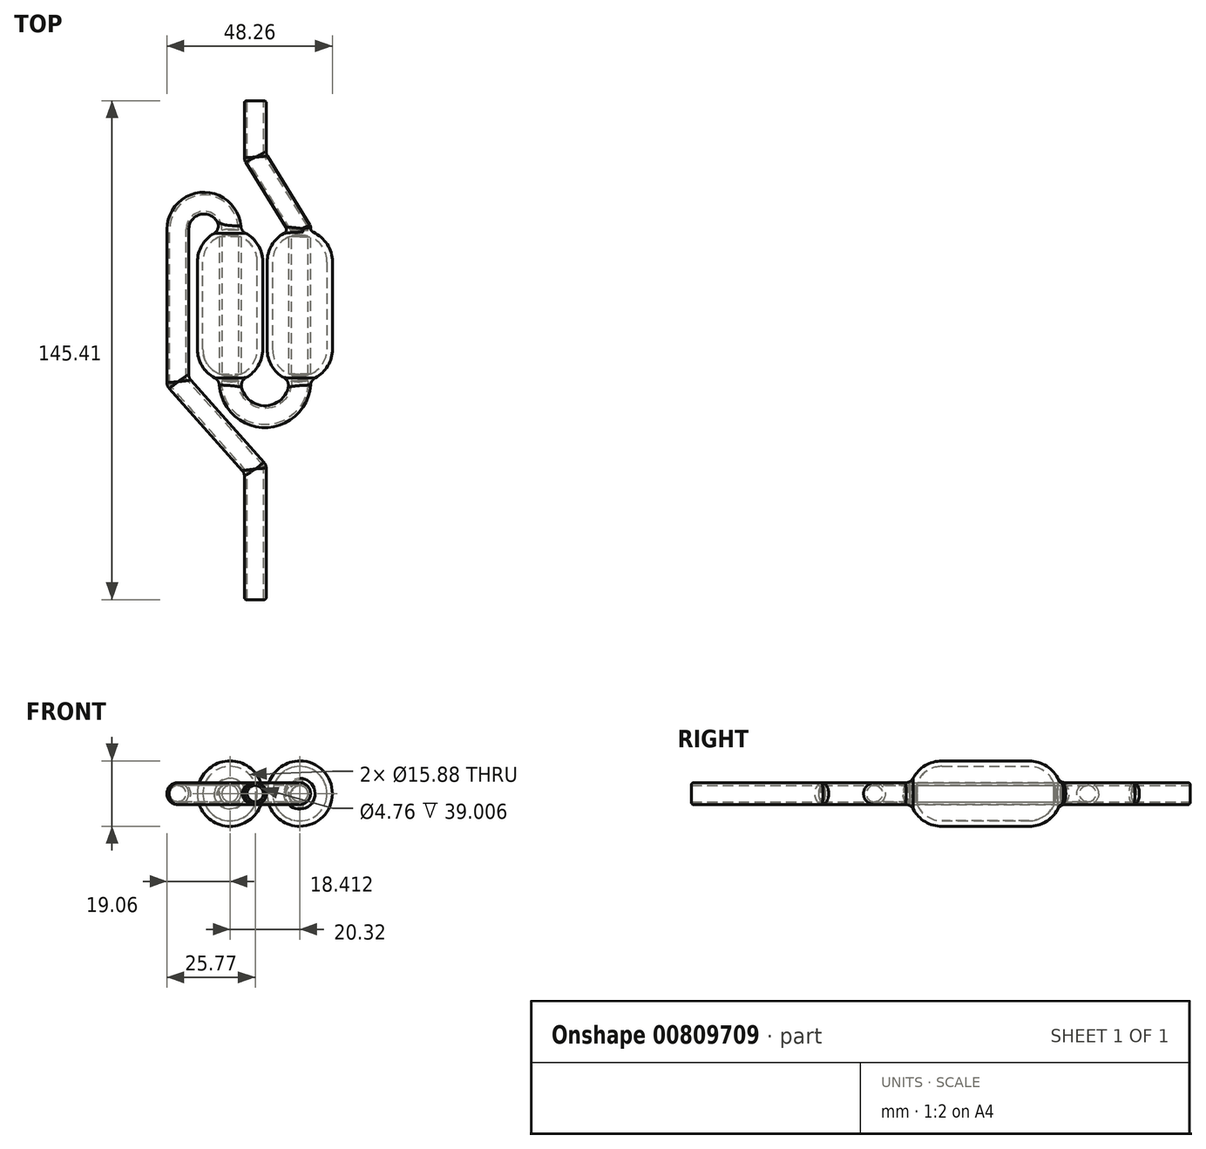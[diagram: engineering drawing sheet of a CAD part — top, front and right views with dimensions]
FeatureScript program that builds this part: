
annotation { "Feature Type Name" : "Feature", "Feature Type Description" : "" }
export const myFeature = defineFeature(function(context is Context, id is Id, definition is map)
    precondition{}
    {
        {
            var Q0;
            Q0=qCreatedBy(makeId("Top.planeOp"),FACE);
            var sketch = newSketch(context, id + "F0", { "sketchPlane" : qUnion([Q0])});
            skLineSegment(sketch, "E0", {"start": v(0, -39.55) * mm, "end": v(0, -1.45) * mm});
            skLineSegment(sketch, "E1", {"start": v(0, -1.45) * mm, "end": v(-22.6, 23.95) * mm});
            skLineSegment(sketch, "E2", {"start": v(-22.6, 23.95) * mm, "end": v(-22.6, 68.4) * mm});
            skLineSegment(sketch, "E3", {"start": v(-7.36, 68.4) * mm, "end": v(-7.36, 23.95) * mm});
            skLineSegment(sketch, "E4", {"start": v(12.96, 23.95) * mm, "end": v(12.96, 68.4) * mm});
            skLineSegment(sketch, "E5", {"start": v(12.96, 68.4) * mm, "end": v(0, 89.43) * mm});
            skLineSegment(sketch, "E6", {"start": v(0, 89.43) * mm, "end": v(0, 105.86) * mm});
            skLineSegment(sketch, "E7", {"start": v(-22.6, 23.95) * mm, "end": v(-14.25, 23.95) * mm, "construction": true});
            skPoint(sketch, "E8.visualSharp", {"position": v(-22.6, 80.08) * mm});
            skArc(sketch, "E8.filletArc", {"start": v(-14.98, 76.02) * mm, "mid": v(-20.37, 73.79) * mm, "end": v(-22.6, 68.4) * mm});
            skPoint(sketch, "E9.visualSharp", {"position": v(-7.36, 76.07) * mm});
            skPoint(sketch, "E10.visualSharp", {"position": v(-14.25, 23.95) * mm});
            skPoint(sketch, "E11.visualSharp", {"position": v(12.96, 3.76) * mm});
            skLineSegment(sketch, "E12", {"start": v(2.17, 58.87) * mm, "end": v(2.17, 33.47) * mm});
            skLineSegment(sketch, "E13", {"start": v(0.58, 58.87) * mm, "end": v(0.58, 33.47) * mm});
            skPoint(sketch, "E14.start.orphan", {"position": v(-14.56, 68.4) * mm});
            skPoint(sketch, "E15.orphan", {"position": v(-13.66, 23.95) * mm});
            skLineSegment(sketch, "E16", {"start": v(12.96, 23.95) * mm, "end": v(12.96, 8.24) * mm, "construction": true});
            skLineSegment(sketch, "E17", {"start": v(12.96, 23.95) * mm, "end": v(20.36, 23.95) * mm, "construction": true});
            skPoint(sketch, "E18.start.orphan", {"position": v(5.98, 68.4) * mm});
            skPoint(sketch, "E19.orphan", {"position": v(7.66, 23.95) * mm});
            skArc(sketch, "E20", {"start": v(-7.36, 23.95) * mm, "mid": v(-0.62, 26.74) * mm, "end": v(2.17, 33.47) * mm});
            skArc(sketch, "E21", {"start": v(0.58, 33.47) * mm, "mid": v(-1.75, 27.86) * mm, "end": v(-7.36, 25.54) * mm});
            skArc(sketch, "E22", {"start": v(-7.36, 68.4) * mm, "mid": v(-0.62, 65.61) * mm, "end": v(2.17, 58.87) * mm});
            skArc(sketch, "E23", {"start": v(0.58, 58.87) * mm, "mid": v(-1.75, 64.49) * mm, "end": v(-7.36, 66.81) * mm});
            skPoint(sketch, "E24.orphan", {"position": v(2.17, 23.95) * mm});
            skPoint(sketch, "E25.orphan", {"position": v(0.58, 68.4) * mm});
            skPoint(sketch, "E26.end.orphan", {"position": v(2.17, 68.4) * mm});
            skLineSegment(sketch, "E27", {"start": v(-7.36, 33.47) * mm, "end": v(0, 33.47) * mm, "construction": true});
            skLineSegment(sketch, "E28", {"start": v(-7.36, 58.87) * mm, "end": v(0, 58.87) * mm, "construction": true});
            skLineSegment(sketch, "E29", {"start": v(12.96, 68.4) * mm, "end": v(12.96, 23.95) * mm});
            skLineSegment(sketch, "E30", {"start": v(22.49, 58.87) * mm, "end": v(22.49, 33.47) * mm});
            skLineSegment(sketch, "E31", {"start": v(20.9, 58.87) * mm, "end": v(20.9, 33.47) * mm});
            skArc(sketch, "E32", {"start": v(12.96, 23.95) * mm, "mid": v(19.7, 26.74) * mm, "end": v(22.49, 33.47) * mm});
            skArc(sketch, "E33", {"start": v(20.9, 33.47) * mm, "mid": v(18.57, 27.86) * mm, "end": v(12.96, 25.54) * mm});
            skArc(sketch, "E34", {"start": v(12.96, 68.4) * mm, "mid": v(19.7, 65.61) * mm, "end": v(22.49, 58.87) * mm});
            skArc(sketch, "E35", {"start": v(20.9, 58.87) * mm, "mid": v(18.57, 64.49) * mm, "end": v(12.96, 66.81) * mm});
            skPoint(sketch, "E36.orphan", {"position": v(22.49, 23.95) * mm});
            skPoint(sketch, "E37.orphan", {"position": v(20.9, 68.4) * mm});
            skPoint(sketch, "E38.end.orphan", {"position": v(22.49, 68.4) * mm});
            skLineSegment(sketch, "E39", {"start": v(12.96, 33.47) * mm, "end": v(20.32, 33.47) * mm, "construction": true});
            skLineSegment(sketch, "E40", {"start": v(12.96, 58.87) * mm, "end": v(20.32, 58.87) * mm, "construction": true});
            skPoint(sketch, "E41.start.orphan", {"position": v(18.68, 68.4) * mm});
            skArc(sketch, "E42", {"start": v(-14.98, 76.02) * mm, "mid": v(-9.6, 73.79) * mm, "end": v(-7.36, 68.4) * mm});
            skPoint(sketch, "E43.end.orphan", {"position": v(-14.98, 76.02) * mm});
            skLineSegment(sketch, "E44", {"start": v(-7.36, 23.95) * mm, "end": v(-22.6, 23.95) * mm, "construction": true});
            skArc(sketch, "E45.MirrorCS", {"start": v(2.8, 13.79) * mm, "mid": v(-4.38, 16.77) * mm, "end": v(-7.36, 23.95) * mm});
            skArc(sketch, "E46.MirrorCS", {"start": v(2.8, 13.79) * mm, "mid": v(9.99, 16.77) * mm, "end": v(12.96, 23.95) * mm});
            skLineSegment(sketch, "E47", {"start": v(-7.36, 23.95) * mm, "end": v(46.58, 23.95) * mm, "construction": true});
            skLineSegment(sketch, "E48", {"start": v(0, 0) * mm, "end": v(0, 151.72) * mm, "construction": true});
            skSolve(sketch);
        }
        {
            var Q0;
            Q0=qCreatedBy(makeId("Front.planeOp"),FACE);
            var Q1;
            Q1=sQuery(id+"F0.wireOp",VERTEX,"E0.start");
            cPlane(context, id + "F1", {"entities" : qUnion([Q0, Q1]), "cplaneType" : CPlaneType.PLANE_POINT, "offset" : 25.4 * mm, "width" : 152.4 * mm, "height" : 152.4 * mm});
        }
        {
            var Q0;
            Q0=qCreatedBy(id+"F1.planeOp",FACE);
            var sketch = newSketch(context, id + "F2", { "sketchPlane" : qUnion([Q0])});
            skCircle(sketch, "E49", {"center": v(0, 0) * mm, "radius": 3.18 * mm});
            skCircle(sketch, "E50", {"center": v(0, 0) * mm, "radius": 2.38 * mm});
            skSolve(sketch);
        }
        {
            var Q0;
            Q0=makeQuery(id+"F2.imprint","IMPRINT",FACE,{"disambiguationData":[TD([[makeQuery(id+"F2.imprint","IMPRINT",EDGE,{"derivedFrom":sQuery(id+"F2.wireOp",EDGE,"E49")}),1.0]])]});
            var Q1;
            Q1=sQuery(id+"F0.wireOp",EDGE,"E0");
            var Q2;
            Q2=sQuery(id+"F0.wireOp",EDGE,"E1");
            var Q3;
            Q3=sQuery(id+"F0.wireOp",EDGE,"E2");
            var Q4;
            Q4=sQuery(id+"F0.wireOp",EDGE,"E8.filletArc");
            var Q5;
            Q5=sQuery(id+"F0.wireOp",EDGE,"E43");
            var Q6;
            Q6=sQuery(id+"F0.wireOp",EDGE,"E9.filletArc");
            var Q7;
            Q7=sQuery(id+"F0.wireOp",EDGE,"E3");
            var Q8;
            Q8=sQuery(id+"F0.wireOp",EDGE,"E10.filletArc");
            var Q9;
            Q9=sQuery(id+"F0.wireOp",EDGE,"5njKzUmd-qnUo-V2Rh-gXgK-mwkRtPWxnCq9");
            var Q10;
            Q10=sQuery(id+"F0.wireOp",EDGE,"E11.filletArc");
            var Q11;
            Q11=sQuery(id+"F0.wireOp",EDGE,"E4");
            var Q12;
            Q12=sQuery(id+"F0.wireOp",EDGE,"E5");
            var Q13;
            Q13=sQuery(id+"F0.wireOp",EDGE,"E6");
            var Q14;
            Q14=sQuery(id+"F0.wireOp",EDGE,"E42");
            var Q15;
            Q15=sQuery(id+"F0.wireOp",EDGE,"E45.MirrorCS");
            var Q16;
            Q16=sQuery(id+"F0.wireOp",EDGE,"E46.MirrorCS");
            sweep(context, id + "F3", {"profiles" : qUnion([Q0]), "path" : qUnion([Q1, Q2, Q3, Q4, Q5, Q6, Q7, Q8, Q9, Q10, Q11, Q12, Q13, Q14, Q15, Q16])});
        }
        {
            var Q0;
            {var subQ0=sQuery(id+"F0.wireOp",EDGE,"E26");Q0=makeQuery(id+"F0.imprint","IMPRINT",FACE,{"disambiguationData":[TD([[makeQuery(id+"F0.imprint","IMPRINT",EDGE,{"derivedFrom":subQ0}),-1.0]])]});}
            var Q1;
            Q1=makeQuery(id+"F0.imprint","IMPRINT",FACE,{"disambiguationData":[TD([[makeQuery(id+"F0.imprint","IMPRINT",EDGE,{"derivedFrom":sQuery(id+"F0.wireOp",EDGE,"E12")}),-1.0]])]});
            var Q2;
            Q2=sQuery(id+"F0.wireOp",EDGE,"E3");
            revolve(context, id + "F4", {"operationType" : NewBodyOperationType.ADD, "surfaceOperationType" : NewSurfaceOperationType.NEW, "entities" : qUnion([Q0, Q1]), "axis" : qUnion([Q2]), "revolveType" : RevolveType.FULL});
        }
        {
            var Q0;
            Q0=makeQuery(id+"F0.imprint","IMPRINT",FACE,{"disambiguationData":[TD([[makeQuery(id+"F0.imprint","IMPRINT",EDGE,{"derivedFrom":sQuery(id+"F0.wireOp",EDGE,"E30")}),-1.0]])]});
            var Q1;
            Q1=sQuery(id+"F0.wireOp",EDGE,"E4");
            revolve(context, id + "F5", {"operationType" : NewBodyOperationType.ADD, "surfaceOperationType" : NewSurfaceOperationType.NEW, "entities" : qUnion([Q0]), "axis" : qUnion([Q1]), "revolveType" : RevolveType.FULL});
        }
        {
            var Q0;
            Q0=makeQuery(id+"F4.boolean.opBoolean","INTERSECT",EDGE,{"derivedFrom":[makeQuery(id+"F3.opSweep","SWEPT_FACE",FACE,{"disambiguationData":[OSD([sQuery(id+"F0.wireOp",EDGE,"E3"),sQuery(id+"F2.wireOp",EDGE,"E49")])]}),makeQuery(id+"F4.opRevolve","SWEPT_FACE",FACE,{"disambiguationData":[OSD([sQuery(id+"F0.wireOp",EDGE,"E22")])]})]});
            var Q1;
            Q1=makeQuery(id+"F4.boolean.opBoolean","INTERSECT",EDGE,{"derivedFrom":[makeQuery(id+"F3.opSweep","SWEPT_FACE",FACE,{"disambiguationData":[OSD([sQuery(id+"F0.wireOp",EDGE,"E3"),sQuery(id+"F2.wireOp",EDGE,"E49")])]}),makeQuery(id+"F4.opRevolve","SWEPT_FACE",FACE,{"disambiguationData":[OSD([sQuery(id+"F0.wireOp",EDGE,"E20")])]})]});
            var Q2;
            Q2=makeQuery(id+"F5.boolean.opBoolean","INTERSECT",EDGE,{"derivedFrom":[makeQuery(id+"F3.opSweep","SWEPT_FACE",FACE,{"disambiguationData":[OSD([sQuery(id+"F0.wireOp",EDGE,"E4"),sQuery(id+"F2.wireOp",EDGE,"E49")])]}),makeQuery(id+"F5.opRevolve","SWEPT_FACE",FACE,{"disambiguationData":[OSD([sQuery(id+"F0.wireOp",EDGE,"E32")])]})]});
            var Q3;
            Q3=makeQuery(id+"F3.opSweep","MID_CAP_EDGE",EDGE,{"disambiguationData":[OSD([sQuery(id+"F0.wireOp",VERTEX,"E2.start"),sQuery(id+"F2.wireOp",EDGE,"E49")])],"capPos":2.0});
            var Q4;
            Q4=makeQuery(id+"F3.opSweep","MID_CAP_EDGE",EDGE,{"disambiguationData":[OSD([sQuery(id+"F0.wireOp",VERTEX,"E1.start"),sQuery(id+"F2.wireOp",EDGE,"E49")])],"capPos":1.0});
            var Q5;
            Q5=makeQuery(id+"F3.opSweep","MID_CAP_EDGE",EDGE,{"disambiguationData":[OSD([sQuery(id+"F0.wireOp",VERTEX,"E6.start"),sQuery(id+"F2.wireOp",EDGE,"E49")])],"capPos":10.0});
            fillet(context, id + "F6", {"entities" : qUnion([Q0, Q1, Q2, Q3, Q4, Q5]), "radius" : 2.54 * mm, "tangentPropagation" : true, "allowEdgeOverflow" : false});
        }
        {
            var Q0;
            Q0=makeQuery(id+"F5.boolean.opBoolean","INTERSECT",EDGE,{"derivedFrom":[makeQuery(id+"F3.opSweep","SWEPT_FACE",FACE,{"disambiguationData":[OSD([sQuery(id+"F0.wireOp",EDGE,"E5"),sQuery(id+"F2.wireOp",EDGE,"E49")])]}),makeQuery(id+"F5.opRevolve","SWEPT_FACE",FACE,{"disambiguationData":[OSD([sQuery(id+"F0.wireOp",EDGE,"E34")])]})]});
            var Q1;
            Q1=makeQuery(id+"F5.boolean.opBoolean","INTERSECT",EDGE,{"derivedFrom":[makeQuery(id+"F3.opSweep","SWEPT_FACE",FACE,{"disambiguationData":[OSD([sQuery(id+"F0.wireOp",EDGE,"E4"),sQuery(id+"F2.wireOp",EDGE,"E49")])]}),makeQuery(id+"F5.opRevolve","SWEPT_FACE",FACE,{"disambiguationData":[OSD([sQuery(id+"F0.wireOp",EDGE,"E34")])]})]});
            fillet(context, id + "F7", {"entities" : qUnion([Q0, Q1]), "radius" : 1.27 * mm, "tangentPropagation" : true, "allowEdgeOverflow" : false});
        }
        {
            var Q0;
            Q0=makeQuery(id+"F3.opSweep","MID_CAP_EDGE",EDGE,{"disambiguationData":[OSD([sQuery(id+"F0.wireOp",VERTEX,"E5.start"),sQuery(id+"F2.wireOp",EDGE,"E49")])],"capPos":9.0});
            var Q1;
            {var subQ0=sQuery(id+"F2.wireOp",EDGE,"E49");var subQ1=makeQuery(id+"F5.opRevolve","SWEPT_FACE",FACE,{"disambiguationData":[OSD([sQuery(id+"F0.wireOp",EDGE,"E34")])]});var subQ2=makeQuery(id+"F3.opSweep","SWEPT_FACE",FACE,{"disambiguationData":[OSD([sQuery(id+"F0.wireOp",EDGE,"E4"),subQ0])]});Q1=makeQuery(id+"F7.opFillet","BLEND_EDGE",EDGE,{"blendedFrom":[makeQuery(id+"F5.boolean.opBoolean","INTERSECT",EDGE,{"derivedFrom":[subQ2,subQ1]}),makeQuery(id+"F5.boolean.opBoolean","SPLIT",FACE,{"disambiguationData":[TD([subQ1])],"derivedFrom":subQ2})],"blendedInto":[makeQuery(id+"F5.boolean.opBoolean","SPLIT",FACE,{"disambiguationData":[TD([subQ1])],"derivedFrom":subQ2})]});}
            fillet(context, id + "F8", {"entities" : qUnion([Q0, Q1]), "radius" : 1.27 * mm, "tangentPropagation" : true, "allowEdgeOverflow" : false});
        }
        {
            var Q0;
            Q0=makeQuery(id+"F3.opSweep","CAP_EDGE",EDGE,{"disambiguationData":[OSD([sQuery(id+"F0.wireOp",VERTEX,"E0.start"),sQuery(id+"F2.wireOp",EDGE,"E49")])],"isStart":true});
            var Q1;
            Q1=makeQuery(id+"F3.opSweep","CAP_EDGE",EDGE,{"disambiguationData":[OSD([sQuery(id+"F0.wireOp",VERTEX,"E6.end"),sQuery(id+"F2.wireOp",EDGE,"E49")])],"isStart":false});
            fillet(context, id + "F9", {"entities" : qUnion([Q0, Q1]), "radius" : 0.64 * mm, "tangentPropagation" : true, "allowEdgeOverflow" : false});
        }
    });
